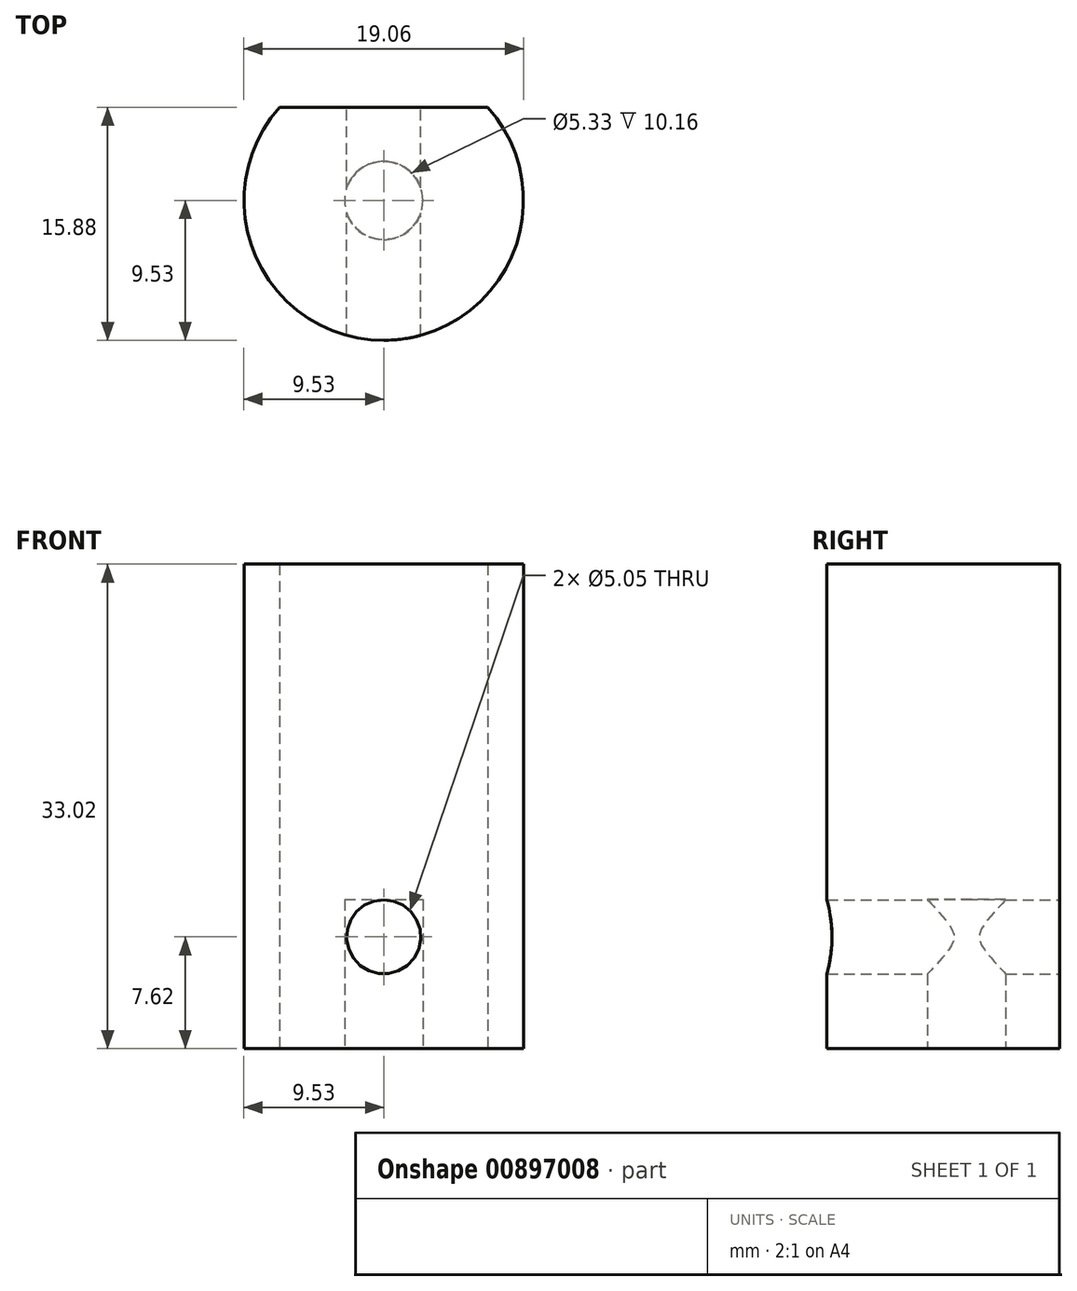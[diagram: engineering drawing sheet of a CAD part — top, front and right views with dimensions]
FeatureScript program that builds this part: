
annotation { "Feature Type Name" : "Feature", "Feature Type Description" : "" }
export const myFeature = defineFeature(function(context is Context, id is Id, definition is map)
    precondition{}
    {
        {
            var Q0;
            Q0=qCreatedBy(makeId("Top.planeOp"),FACE);
            var sketch = newSketch(context, id + "F0", { "sketchPlane" : qUnion([Q0])});
            skArc(sketch, "E0", {"start": v(-7.1, 6.35) * mm, "mid": v(0, -9.53) * mm, "end": v(7.1, 6.35) * mm});
            skLineSegment(sketch, "E1", {"start": v(0, 9.53) * mm, "end": v(0, 6.35) * mm, "construction": true});
            skLineSegment(sketch, "E2", {"start": v(7.1, 6.35) * mm, "end": v(-7.1, 6.35) * mm});
            skSolve(sketch);
        }
        {
            var Q0;
            Q0 = qSketchRegion(id + "F0", true);
            extrude(context, id + "F1", {"entities" : qUnion([Q0]), "depth" : 33.02 * mm, "offsetDistance" : 25.4 * mm});
        }
        {
            var Q0;
            Q0=makeQuery(id+"F1.opExtrude","SWEPT_FACE",FACE,{"disambiguationData":[OSD([sQuery(id+"F0.wireOp",EDGE,"E2")])]});
            var sketch = newSketch(context, id + "F2", { "sketchPlane" : qUnion([Q0])});
            skCircle(sketch, "E3", {"center": v(0, 7.62) * mm, "radius": 2.53 * mm});
            skPoint(sketch, "E3.centerSnap0", {"position": v(0, 0) * mm});
            skSolve(sketch);
        }
        {
            var Q0;
            Q0 = qSketchRegion(id + "F2", true);
            extrude(context, id + "F3", {"entities" : qUnion([Q0]), "operationType" : NewBodyOperationType.REMOVE, "oppositeDirection" : true, "depth" : 25.4 * mm, "offsetDistance" : 25.4 * mm});
        }
        {
            var Q0;
            Q0=makeQuery(id+"F1.opExtrude","CAP_FACE",FACE,{"disambiguationData":[OSD([sQuery(id+"F0.wireOp",EDGE,"E0"),sQuery(id+"F0.wireOp",EDGE,"E2")])],"isStart":true});
            var sketch = newSketch(context, id + "F4", { "sketchPlane" : qUnion([Q0])});
            skCircle(sketch, "E4", {"center": v(0, 0) * mm, "radius": 2.67 * mm});
            skSolve(sketch);
        }
        {
            var Q0;
            Q0 = qSketchRegion(id + "F4", true);
            extrude(context, id + "F5", {"entities" : qUnion([Q0]), "operationType" : NewBodyOperationType.REMOVE, "oppositeDirection" : true, "depth" : 10.16 * mm, "offsetDistance" : 25.4 * mm});
        }
    });
